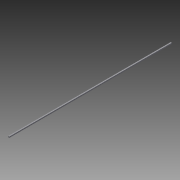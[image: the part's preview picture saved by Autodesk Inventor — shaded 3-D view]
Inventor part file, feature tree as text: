
AUTODESK INVENTOR PART (.ipt)
format: ipt  version: 2014 (Build 180170000, 170)  size: 67,584 bytes
history: native  units: in
note: dims shown in document units (in); Inventor stores cm internally (conversion verified against a paired STEP export)
features: extrude x1, sketch x1
ambient origin geometry x8: Origin, YZ Plane, XZ Plane, XY Plane, X Axis, Y Axis, Z Axis, Center Point
bodies: Solid1 (feature_tree)
feature tree (2):
  extrude  "Extrusion1"  Depth=36.75in
  sketch  "Sketch1"  dims[d0=0.25in d1=36.75in d2=0.25in d3=0.0in]
